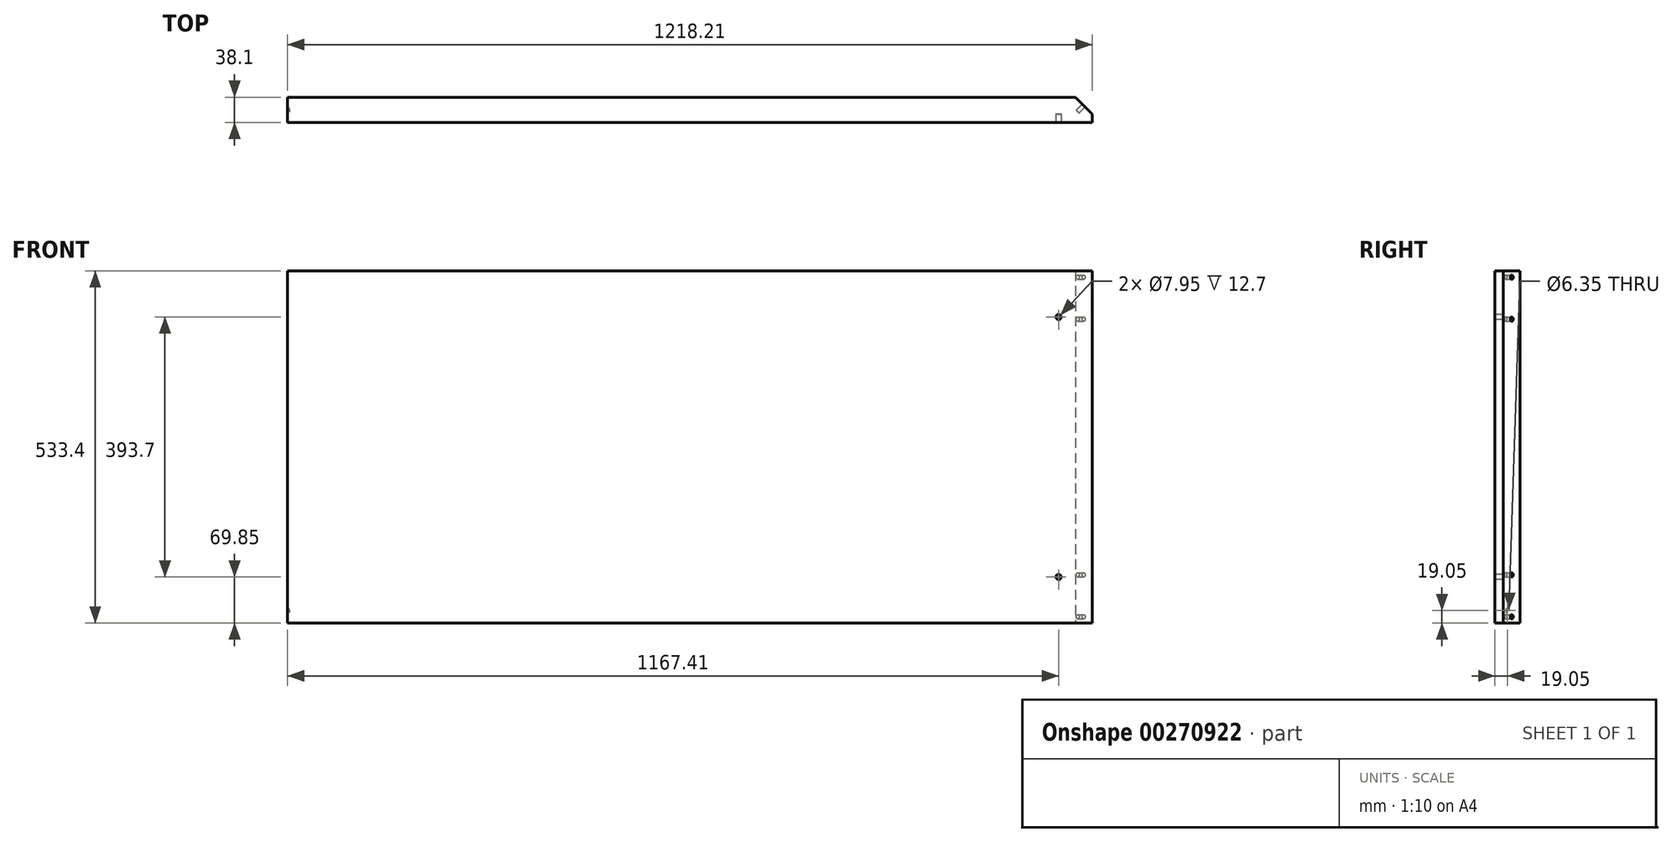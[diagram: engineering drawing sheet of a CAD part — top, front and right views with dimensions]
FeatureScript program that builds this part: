
annotation { "Feature Type Name" : "Feature", "Feature Type Description" : "" }
export const myFeature = defineFeature(function(context is Context, id is Id, definition is map)
    precondition{}
    {
        {
            var Q0;
            Q0=qCreatedBy(makeId("Front.planeOp"),FACE);
            var sketch = newSketch(context, id + "F0", { "sketchPlane" : qUnion([Q0])});
            skLineSegment(sketch, "E0.top", {"start": v(0, -571.5) * mm, "end": v(1218.2, -571.5) * mm});
            skLineSegment(sketch, "E0.left", {"start": v(0, -38.1) * mm, "end": v(0, -571.5) * mm});
            skLineSegment(sketch, "E0.right", {"start": v(1218.2, -38.1) * mm, "end": v(1218.2, -571.5) * mm});
            skPoint(sketch, "E1.orphan", {"position": v(0, 0) * mm});
            skLineSegment(sketch, "E2", {"start": v(0, -6.35) * mm, "end": v(0, 0) * mm});
            skLineSegment(sketch, "E3", {"start": v(1218.2, -6.35) * mm, "end": v(1218.2, 0) * mm});
            skLineSegment(sketch, "E4", {"start": v(0, 0) * mm, "end": v(0, -6.35) * mm});
            skLineSegment(sketch, "E5", {"start": v(0, -38.1) * mm, "end": v(1218.2, -38.1) * mm});
            skSolve(sketch);
        }
        {
            var Q0;
            Q0 = qSketchRegion(id + "F0", true);
            extrude(context, id + "F1", {"entities" : qUnion([Q0]), "depth" : 38.1 * mm});
        }
        {
            var Q0;
            Q0=makeQuery(id+"F1.opExtrude","SWEPT_FACE",FACE,{"disambiguationData":[OSD([sQuery(id+"F0.wireOp",EDGE,"E0.left")])]});
            var sketch = newSketch(context, id + "F2", { "sketchPlane" : qUnion([Q0])});
            skLineSegment(sketch, "E6.bottom", {"start": v(0, -571.5) * mm, "end": v(38.1, -571.5) * mm});
            skLineSegment(sketch, "E6.top", {"start": v(0, -609.6) * mm, "end": v(38.1, -609.6) * mm});
            skLineSegment(sketch, "E6.left", {"start": v(0, -571.5) * mm, "end": v(0, -609.6) * mm});
            skLineSegment(sketch, "E6.right", {"start": v(38.1, -571.5) * mm, "end": v(38.1, -609.6) * mm});
            skLineSegment(sketch, "E7", {"start": v(19.05, -609.6) * mm, "end": v(19.05, -590.55) * mm});
            skPoint(sketch, "E7.endSnap0", {"position": v(0, -590.55) * mm});
            skLineSegment(sketch, "E8.top", {"start": v(0, -533.4) * mm, "end": v(38.1, -533.4) * mm});
            skLineSegment(sketch, "E8.left", {"start": v(0, -571.5) * mm, "end": v(0, -533.4) * mm});
            skLineSegment(sketch, "E8.right", {"start": v(38.1, -571.5) * mm, "end": v(38.1, -533.4) * mm});
            skLineSegment(sketch, "E9", {"start": v(19.05, -571.5) * mm, "end": v(19.05, -552.45) * mm});
            skPoint(sketch, "E9.endSnap0", {"position": v(0, -552.45) * mm});
            skLineSegment(sketch, "E10.MirrorCS", {"start": v(0, -495.3) * mm, "end": v(38.1, -495.3) * mm});
            skLineSegment(sketch, "E11.MirrorCS", {"start": v(0, -495.3) * mm, "end": v(0, -533.4) * mm});
            skLineSegment(sketch, "E12.MirrorCS", {"start": v(38.1, -495.3) * mm, "end": v(38.1, -533.4) * mm});
            skLineSegment(sketch, "E13.MirrorCS", {"start": v(19.05, -495.3) * mm, "end": v(19.05, -514.35) * mm});
            skLineSegment(sketch, "E14", {"start": v(0, -304.8) * mm, "end": v(38.1, -304.8) * mm});
            skLineSegment(sketch, "E15.MirrorCS", {"start": v(0, -76.2) * mm, "end": v(38.1, -76.2) * mm});
            skLineSegment(sketch, "E16.MirrorCS", {"start": v(38.1, -38.1) * mm, "end": v(38.1, -76.2) * mm});
            skLineSegment(sketch, "E17.MirrorCS", {"start": v(0, -38.1) * mm, "end": v(0, -76.2) * mm});
            skLineSegment(sketch, "E18.MirrorCS", {"start": v(0, -38.1) * mm, "end": v(38.1, -38.1) * mm});
            skLineSegment(sketch, "E19.MirrorCS", {"start": v(19.05, -38.1) * mm, "end": v(19.05, -57.15) * mm});
            skSolve(sketch);
        }
        {
            var Q0;
            Q0=sQuery(id+"F2.wireOp",VERTEX,"E9.end");
            var Q1;
            Q1=sQuery(id+"F2.wireOp",VERTEX,"E7.end");
            var Q2;
            Q2=makeQuery(id+"F1.opExtrude","SWEPT_BODY",BODY,{"disambiguationData":[OSD([sQuery(id+"F0.wireOp",EDGE,"E0.top"),sQuery(id+"F0.wireOp",EDGE,"E0.left"),sQuery(id+"F0.wireOp",EDGE,"E0.right"),sQuery(id+"F0.wireOp",EDGE,"gDhKNAhB-mvM7-LPII-0QTI-d5j6MYJOtABQ")])]});
            hole(context, id + "F3", {"style" : HoleStyle.SIMPLE, "endStyle" : HoleEndStyle.BLIND, "holeDiameter" : 6.35 * mm, "holeDepth" : 1.52 * mm, "tappedDepth" : 12.7 * mm, "tapClearance" : 3, "locations" : qUnion([Q0, Q1]), "scope" : qUnion([Q2])});
        }
        {
            var Q0;
            Q0=makeQuery(id+"F1.opExtrude","CAP_EDGE",EDGE,{"disambiguationData":[OSD([sQuery(id+"F0.wireOp",EDGE,"E0.right"),sQuery(id+"F0.wireOp",EDGE,"E3")])],"isStart":true});
            chamfer(context, id + "F4", {"entities" : qUnion([Q0]), "chamferType" : ChamferType.OFFSET_ANGLE, "width" : 25.4 * mm, "oppositeDirection" : false, "angle" : 45 * degree, "tangentPropagation" : true});
        }
        {
            var Q0;
            Q0=makeQuery(id+"F4.opChamfer","BLEND_FACE",FACE,{"disambiguationData":[OSD([sQuery(id+"F0.wireOp",EDGE,"E0.right"),sQuery(id+"F0.wireOp",EDGE,"E3")])]});
            var sketch = newSketch(context, id + "F5", { "sketchPlane" : qUnion([Q0])});
            skLineSegment(sketch, "E20", {"start": v(-861.4, -571.5) * mm, "end": v(-861.4, 0) * mm});
            skLineSegment(sketch, "E21", {"start": v(-879.36, -304.8) * mm, "end": v(-843.44, -304.8) * mm});
            skLineSegment(sketch, "E22", {"start": v(-879.36, -571.5) * mm, "end": v(-879.36, -561.98) * mm});
            skLineSegment(sketch, "E23", {"start": v(-879.36, -561.98) * mm, "end": v(-861.4, -561.98) * mm});
            skLineSegment(sketch, "E24", {"start": v(-861.4, -561.98) * mm, "end": v(-861.4, -498.47) * mm});
            skCircle(sketch, "E25", {"center": v(-861.4, -561.98) * mm, "radius": 3.18 * mm});
            skCircle(sketch, "E26", {"center": v(-861.4, -498.47) * mm, "radius": 3.18 * mm});
            skCircle(sketch, "E27.MirrorC", {"center": v(-861.4, -111.12) * mm, "radius": 3.18 * mm});
            skCircle(sketch, "E28.MirrorC", {"center": v(-861.4, -47.62) * mm, "radius": 3.18 * mm});
            skSolve(sketch);
        }
        {
            var Q0;
            Q0 = qSketchRegion(id + "F5", true);
            extrude(context, id + "F6", {"entities" : qUnion([Q0]), "operationType" : NewBodyOperationType.REMOVE, "oppositeDirection" : true, "depth" : 12.7 * mm});
        }
        {
            var Q0;
            Q0=makeQuery(id+"F1.opExtrude","CAP_FACE",FACE,{"disambiguationData":[OSD([sQuery(id+"F0.wireOp",EDGE,"E0.top"),sQuery(id+"F0.wireOp",EDGE,"E0.left"),sQuery(id+"F0.wireOp",EDGE,"E0.right"),sQuery(id+"F0.wireOp",EDGE,"E2"),sQuery(id+"F0.wireOp",EDGE,"E3"),sQuery(id+"F0.wireOp",EDGE,"OJToeVrM-cnnJ-DGrI-Unpg-SY5Kk1vZ85yR")])],"isStart":false});
            var sketch = newSketch(context, id + "F7", { "sketchPlane" : qUnion([Q0])});
            skLineSegment(sketch, "E29", {"start": v(1218.2, 0) * mm, "end": v(1167.4, 0) * mm});
            skLineSegment(sketch, "E30", {"start": v(1167.4, 0) * mm, "end": v(1167.4, -107.95) * mm});
            skCircle(sketch, "E31", {"center": v(1167.4, -107.95) * mm, "radius": 3.98 * mm});
            skLineSegment(sketch, "E32", {"start": v(1218.2, -304.8) * mm, "end": v(1008.9, -304.8) * mm});
            skCircle(sketch, "E33.MirrorC", {"center": v(1167.4, -501.65) * mm, "radius": 3.98 * mm});
            skLineSegment(sketch, "E34", {"start": v(1218.2, 0) * mm, "end": v(1218.2, -38.1) * mm});
            skSolve(sketch);
        }
        {
            var Q0;
            Q0 = qSketchRegion(id + "F7", true);
            extrude(context, id + "F8", {"entities" : qUnion([Q0]), "operationType" : NewBodyOperationType.REMOVE, "oppositeDirection" : true, "depth" : 12.7 * mm});
        }
    });
